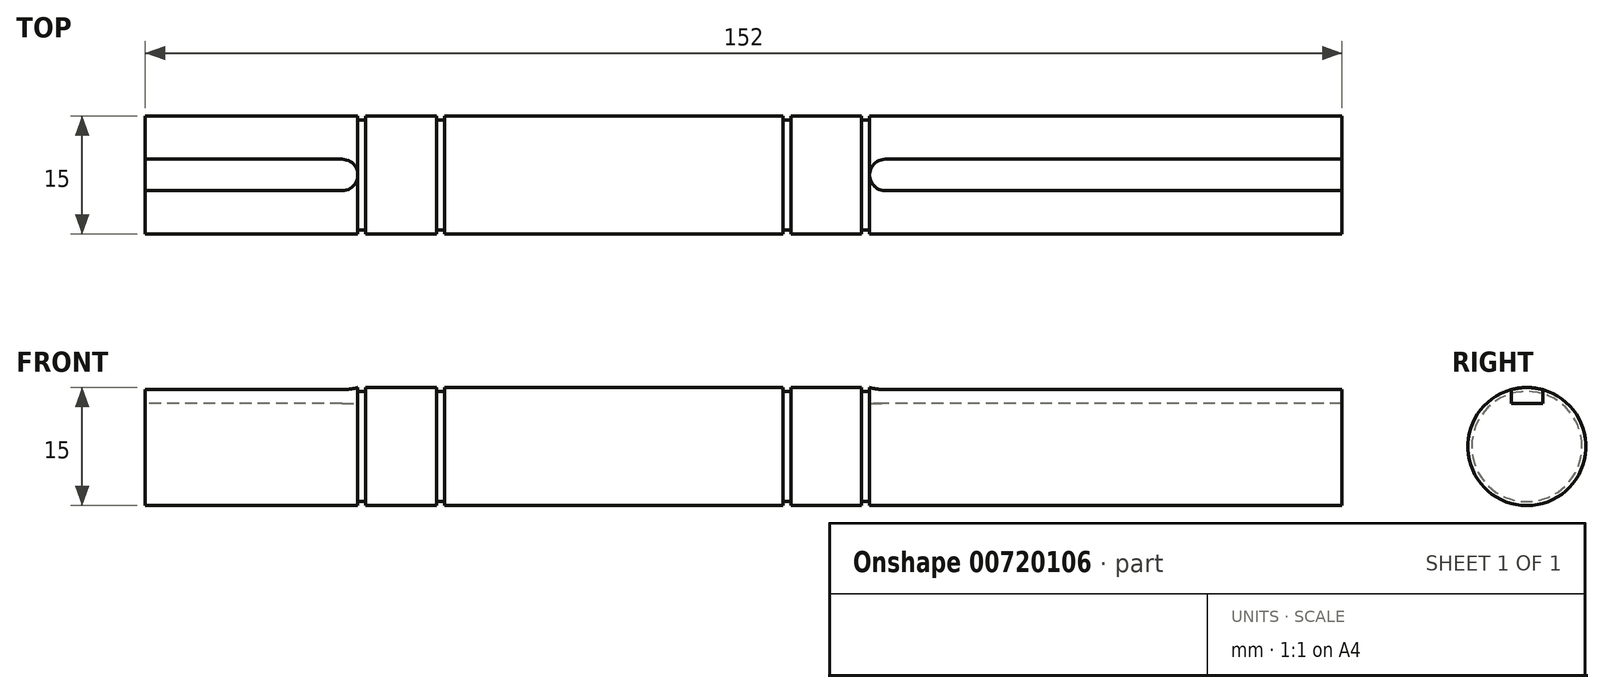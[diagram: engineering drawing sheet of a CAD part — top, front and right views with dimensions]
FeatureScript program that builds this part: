
annotation { "Feature Type Name" : "Feature", "Feature Type Description" : "" }
export const myFeature = defineFeature(function(context is Context, id is Id, definition is map)
    precondition{}
    {
        {
            var Q0;
            Q0=qCreatedBy(makeId("Front.planeOp"),FACE);
            var sketch = newSketch(context, id + "F0", { "sketchPlane" : qUnion([Q0])});
            skLineSegment(sketch, "E0", {"start": v(0, 0) * mm, "end": v(0, 7.5) * mm});
            skLineSegment(sketch, "E1", {"start": v(0, 7.5) * mm, "end": v(27, 7.5) * mm});
            skLineSegment(sketch, "E2", {"start": v(27, 7.5) * mm, "end": v(27, 7) * mm});
            skLineSegment(sketch, "E3", {"start": v(27, 7) * mm, "end": v(28, 7) * mm});
            skLineSegment(sketch, "E4", {"start": v(28, 7) * mm, "end": v(28, 7.5) * mm});
            skLineSegment(sketch, "E5", {"start": v(28, 7.5) * mm, "end": v(37, 7.5) * mm});
            skLineSegment(sketch, "E6", {"start": v(37, 7.5) * mm, "end": v(37, 7) * mm});
            skLineSegment(sketch, "E7", {"start": v(37, 7) * mm, "end": v(38, 7) * mm});
            skLineSegment(sketch, "E8", {"start": v(38, 7) * mm, "end": v(38, 7.5) * mm});
            skLineSegment(sketch, "E9", {"start": v(38, 7.5) * mm, "end": v(81, 7.5) * mm});
            skLineSegment(sketch, "E10", {"start": v(81, 7.5) * mm, "end": v(81, 7) * mm});
            skLineSegment(sketch, "E11", {"start": v(81, 7) * mm, "end": v(82, 7) * mm});
            skLineSegment(sketch, "E12", {"start": v(82, 7) * mm, "end": v(82, 7.5) * mm});
            skLineSegment(sketch, "E13", {"start": v(82, 7.5) * mm, "end": v(91, 7.5) * mm});
            skLineSegment(sketch, "E14", {"start": v(91, 7.5) * mm, "end": v(91, 7) * mm});
            skLineSegment(sketch, "E15", {"start": v(91, 7) * mm, "end": v(92, 7) * mm});
            skLineSegment(sketch, "E16", {"start": v(92, 7) * mm, "end": v(92, 7.5) * mm});
            skLineSegment(sketch, "E17", {"start": v(92, 7.5) * mm, "end": v(152, 7.5) * mm});
            skLineSegment(sketch, "E18", {"start": v(152, 7.5) * mm, "end": v(152, 0) * mm});
            skLineSegment(sketch, "E19", {"start": v(152, 0) * mm, "end": v(0, 0) * mm});
            skSolve(sketch);
        }
        {
            var Q0;
            Q0=makeQuery(id+"F0.imprint","IMPRINT",FACE,{"disambiguationData":[TD([[makeQuery(id+"F0.imprint","IMPRINT",EDGE,{"derivedFrom":sQuery(id+"F0.wireOp",EDGE,"E0")}),-1.0]])]});
            var Q1;
            Q1=sQuery(id+"F0.wireOp",EDGE,"E19");
            revolve(context, id + "F1", {"surfaceOperationType" : NewSurfaceOperationType.NEW, "entities" : qUnion([Q0]), "axis" : qUnion([Q1]), "revolveType" : RevolveType.FULL});
        }
        {
            var Q0;
            Q0=qCreatedBy(makeId("Top.planeOp"),FACE);
            cPlane(context, id + "F2", {"entities" : qUnion([Q0]), "cplaneType" : CPlaneType.OFFSET, "offset" : 7.5 * mm, "width" : 150 * mm, "height" : 150 * mm});
        }
        {
            var Q0;
            Q0=qCreatedBy(id+"F2.planeOp",FACE);
            var sketch = newSketch(context, id + "F3", { "sketchPlane" : qUnion([Q0])});
            skLineSegment(sketch, "E20", {"start": v(0, 0) * mm, "end": v(0, 2) * mm});
            skLineSegment(sketch, "E21", {"start": v(0, 2) * mm, "end": v(25, 2) * mm});
            skLineSegment(sketch, "E22", {"start": v(25, -2) * mm, "end": v(0, -2) * mm});
            skLineSegment(sketch, "E23", {"start": v(0, -2) * mm, "end": v(0, 0) * mm});
            skArc(sketch, "E24", {"start": v(25, -2) * mm, "mid": v(27, 0) * mm, "end": v(25, 2) * mm});
            skLineSegment(sketch, "E25", {"start": v(152, 0) * mm, "end": v(152, 2) * mm});
            skLineSegment(sketch, "E26", {"start": v(152, 2) * mm, "end": v(94, 2) * mm});
            skLineSegment(sketch, "E27", {"start": v(152, -2) * mm, "end": v(152, 0) * mm});
            skLineSegment(sketch, "E28", {"start": v(152, -2) * mm, "end": v(94, -2) * mm});
            skArc(sketch, "E29", {"start": v(94, 2) * mm, "mid": v(92, 0) * mm, "end": v(94, -2) * mm});
            skPoint(sketch, "E29.centerSnap0", {"position": v(92, 0) * mm});
            skSolve(sketch);
        }
        {
            var Q0;
            Q0 = qSketchRegion(id + "F3", true);
            extrude(context, id + "F4", {"entities" : qUnion([Q0]), "operationType" : NewBodyOperationType.REMOVE, "oppositeDirection" : true, "depth" : 2 * mm, "offsetDistance" : 25 * mm});
        }
    });
